# Revit family: Вентилятор круглый пластиковый V
name_source: partatom
category: Оборудование
units: mm (PartAtom-declared; Revit-internal decimal feet)

## family parameters
Всегда вертикально = Да
Заголовок OmniClass = Climate Control (HVAC)
На основе рабочей плоскости = Нет
Номер OmniClass = 23.75.00.00
Общий = Нет
При загрузке вырезать с полостями = Нет
Размер круглого соединителя = Использовать диаметр
Тип детали = Нормальный
Точка расчета площади = Нет

## types (6) — shared parameters
s = 30 мм
Единица измерения = шт.
Завод изготовитель = Naveka
Наименование и тех.хар-ка = Вентилятор в пластиковом корпусе для круглого канала
Напряжение U,В = 1-220
Примечание = https://progress-nw.ru

## per-type parameters (varying)
| type | D | D1 | L | R | q | r | Масса единицы | Материал | Мощность двигателя N,Вт | Сила тока J, А | Частота вращения n, об/мин |
| V-100 | 126 мм | 100 мм | 215 мм | 50 мм | 55 мм | 49 мм | 3.2 кг | Сталь серая | 52 | 0.23 | 2350 |
| V-125 | 126 мм | 125 мм | 220 мм | 63 мм | 68 мм | 62 мм | 3.7 кг | Сталь серая | 52 | 0.23 | 2350 |
| V-160 | 170 мм | 160 мм | 229 мм | 80 мм | 85 мм | 79 мм | 4.1 кг | Сталь серая | 85 | 0.38 | 2700 |
| V-200 | 170 мм | 200 мм | 250 мм | 100 мм | 105 мм | 99 мм | 4.8 кг | Сталь серая | 135 | 0.6 | 2650 |
| V-250 | 170 мм | 250 мм | 250 мм | 125 мм | 130 мм | 124 мм | 5.1 кг | Пластмасса, непрозрачная, белая | 210 | 0.93 | 2500 |
| V-315B | 203 мм | 315 мм | 284 мм | 158 мм | 163 мм | 157 мм | 6.1 кг | Сталь серая | 225 | 1.0 | 2700 |

note: column(s) folded — value = type name in every type: Тип, марка, обозначение
